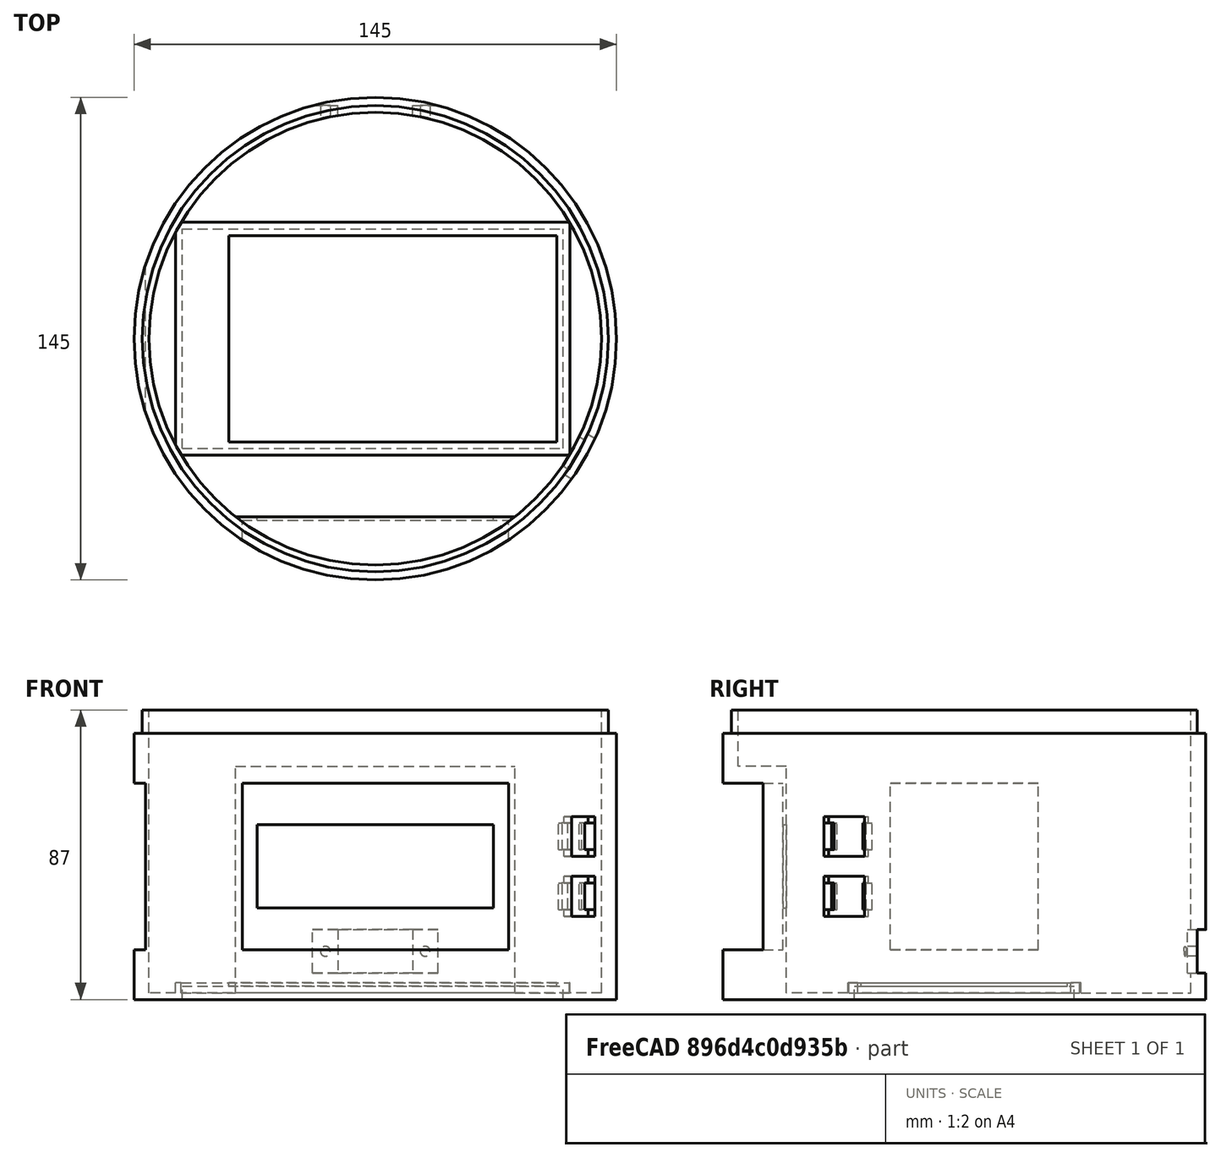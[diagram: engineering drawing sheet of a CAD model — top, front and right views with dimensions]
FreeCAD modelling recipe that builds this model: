
FCSTD DOCUMENT  (FreeCAD 0.16R)
Label: housing
License: All rights reserved
LicenseURL: http://en.wikipedia.org/wiki/All_rights_reserved
objects: Part::Cut×17, Part::Box×15, Part::Cylinder×5, Part::MultiFuse×3, Part::MultiCommon×1
note: 41 computed .brp shape members not serialized (recipe doc carries the construction recipe); baked Part::Feature solids carry a one-line shape summary decoded from their .brp

FEATURE [Part::Cylinder] Cylinder  label="base"
  Angle = 360
  Height = 80
  Radius = 72.5
FEATURE [Part::Cylinder] Cylinder001  label="wall"
  Angle = 360
  Height = 87
  Radius = 70
FEATURE [Part::Cylinder] Cylinder002  label="base_cutout"
  Angle = 360
  Height = 85
  Placement = pos=(0,0,2) rot=(0,0,1;0rad)
  Radius = 68
FEATURE [Part::MultiFuse] Fusion
  Shapes = -> [Cylinder,Cylinder001]
FEATURE [Part::Cut] Cut
  Base = -> Fusion
  Tool = -> Cylinder002
FEATURE [Part::Box] Box  label="display_fillup"
  Height = 70
  Length = 84
  Placement = pos=(-42,-83.5,0) rot=(0,0,1;0rad)
  Width = 30
FEATURE [Part::Box] Box001  label="display_cutout_big"
  Height = 50
  Length = 80
  Placement = pos=(-40,-84.5,15) rot=(0,0,1;0rad)
  Width = 30
FEATURE [Part::MultiCommon] Common
  Shapes = -> [Fusion,Box]
FEATURE [Part::MultiFuse] Fusion001
  Shapes = -> [Cut,Common]
FEATURE [Part::Cut] Cut001
  Base = -> Fusion001
  Tool = -> Box001
FEATURE [Part::Box] Box002  label="inner_dsp_cutout"
  Height = 25
  Length = 71
  Placement = pos=(-35.5,-59,27.5) rot=(0,0,1;0rad)
  Width = 10
FEATURE [Part::Cut] Cut002
  Base = -> Cut001
  Tool = -> Box002
FEATURE [Part::Box] Box004  label="button_cutout_2"
  Height = 12
  Length = 14
  Placement = pos=(67,-47,43) rot=(0,0,1;1.02974rad)
  Width = 12
FEATURE [Part::Box] Box006  label="button_cutout_004"
  Height = 12
  Length = 14
  Placement = pos=(67,-47,25) rot=(0,0,1;1.02974rad)
  Width = 12
FEATURE [Part::Cut] Cut003
  Base = -> Cut002
  Tool = -> Box004
FEATURE [Part::Cut] Cut004
  Base = -> Cut003
  Tool = -> Box006
FEATURE [Part::Box] Box007  label="rfid_cutout"
  Height = 50
  Length = 10
  Placement = pos=(-79,-22.5,15) rot=(0,0,1;0rad)
  Width = 45
FEATURE [Part::Cut] Cut005
  Base = -> Cut004
  Tool = -> Box007
FEATURE [Part::Box] Box008  label="pin1_cutout"
  Height = 8
  Length = 2
  Placement = pos=(62,-44,27) rot=(0,0,1;1.02974rad)
  Width = 10
FEATURE [Part::Box] Box009  label="pin2_cutout"
  Height = 8
  Length = 2
  Placement = pos=(67,-33,27) rot=(0,0,1;1.02974rad)
  Width = 10
FEATURE [Part::Box] Box010  label="pin2_cutout001"
  Height = 8
  Length = 2
  Placement = pos=(67,-33,45) rot=(0,0,1;1.02974rad)
  Width = 10
FEATURE [Part::Box] Box011  label="pin1_cutout001"
  Height = 8
  Length = 2
  Placement = pos=(62,-44,45) rot=(0,0,1;1.02974rad)
  Width = 10
FEATURE [Part::Cut] Cut006
  Base = -> Cut005
  Tool = -> Box008
FEATURE [Part::Cut] Cut007
  Base = -> Cut006
  Tool = -> Box009
FEATURE [Part::Cut] Cut008
  Base = -> Cut007
  Tool = -> Box011
FEATURE [Part::Cut] Cut009
  Base = -> Cut008
  Tool = -> Box010
FEATURE [Part::Box] Box012  label="battery_cutout001"
  Height = 4
  Length = 114.5
  Placement = pos=(-58,-33,0) rot=(0,0,1;0rad)
  Width = 66
FEATURE [Part::Box] Box013  label="battery_cutout"
  Height = 10
  Length = 98.5
  Placement = pos=(-44,-31,0) rot=(0,0,1;0rad)
  Width = 62
FEATURE [Part::Box] Box014  label="battery_fillup"
  Height = 5
  Length = 118.5
  Placement = pos=(-60,-35,0) rot=(0,0,1;0rad)
  Width = 70
FEATURE [Part::MultiFuse] Fusion002
  Shapes = -> [Cut009,Box014]
FEATURE [Part::Cut] Cut010
  Base = -> Fusion002
  Tool = -> Box012
FEATURE [Part::Cut] Cut011
  Base = -> Cut010
  Tool = -> Box013
FEATURE [Part::Box] Box015  label="PowerSwitch"
  Height = 13
  Length = 38
  Placement = pos=(-19,70,8) rot=(0,0,1;0rad)
  Width = 10
FEATURE [Part::Cut] Cut012
  Base = -> Cut011
  Tool = -> Box015
FEATURE [Part::Box] Box016  label="PowerCutout"
  Height = 13
  Length = 22.5
  Placement = pos=(-11.25,63,8) rot=(0,0,1;0rad)
  Width = 13
FEATURE [Part::Cut] Cut013
  Base = -> Cut012
  Tool = -> Box015
FEATURE [Part::Cut] Cut014
  Base = -> Cut013
  Tool = -> Box016
FEATURE [Part::Cylinder] Cylinder003  label="ScrewCutout1"
  Angle = 360
  Height = 10
  Placement = pos=(15,73,14.5) rot=(1,0,0;1.5708rad)
  Radius = 1.5
FEATURE [Part::Cylinder] Cylinder004  label="ScrewCutout002"
  Angle = 360
  Height = 10
  Placement = pos=(-15,73,14.5) rot=(1,0,0;1.5708rad)
  Radius = 1.5
FEATURE [Part::Cut] Cut015
  Base = -> Cut014
  Tool = -> Cylinder003
FEATURE [Part::Cut] Cut016
  Base = -> Cut015
  Tool = -> Cylinder004
